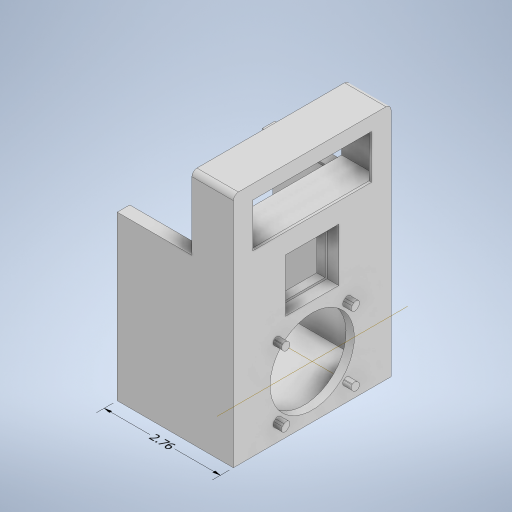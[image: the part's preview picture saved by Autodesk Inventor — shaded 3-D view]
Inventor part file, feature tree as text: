
AUTODESK INVENTOR PART (.ipt)
format: ipt  version: 2024 (Build 280153000, 153)  size: 946,688 bytes
history: native  units: in
note: dims shown in document units (in); Inventor stores cm internally (conversion verified against a paired STEP export)
features: extrude x9, sketch x7, other x2, projected_geometry x2, shell x1, fillet x1
ambient origin geometry x8: Origin, YZ Plane, XZ Plane, XY Plane, X Axis, Y Axis, Z Axis, Center Point
bodies: Solid1 (feature_tree)
feature tree (22):
  other  "Annotations"
  sketch  "Sketch1"  dims[d0=2.0709in d1=2.0709in]
  extrude  "Extrusion1"  Depth=2.0709in
  extrude  "Extrusion2"  Depth=1.2598in
  extrude  "Extrusion4"  Depth=0.8268in
  extrude  "Extrusion5"  Depth=0.2126in
  extrude  "Extrusion6"  Depth=0.0787in
  shell  "Shell2"  Thickness=1.5748in
  extrude  "Extrusion7"  Depth=2.815in
  extrude  "Extrusion8"  Depth=2.7559in
  extrude  "Extrusion9"  Depth=2.7559in
  extrude  "Extrusion10"  Depth=1.7323in
  fillet  "Fillet1"  Radius=3.7402in
  sketch  "Sketch2"  dims[d2=1.2598in d3=1.2598in]
  sketch  "Sketch3"  dims[d4=2.0in d5=0.8268in]
  sketch  "Sketch4"  dims[d6=0.8268in d7=0.2126in]
  projected_geometry  "Projected Loop1"
  sketch  "Sketch5"  dims[d8=0.1732in d9=0.0787in d10=1.5748in d12=360.0deg]
  sketch  "Sketch6"  dims[d15=0.1969in d16=2.815in]
  projected_geometry  "Projected Loop2"
  sketch  "Sketch7"  dims[d17=1.0433in d18=1.8701in d19=1.8701in d20=1.7323in d21=3.7402in d22=2.7559in d23=0.0in d25=0.1969in d26=0.0in d27=3.3661in d28=1.1811in d31=0.0591in d32=0.0in d33=0.0591in d34=0.0in d35=0.9843in d36=0.0in d37=0.0492in d38=2.5591in d39=0.0in d40=2.4803in d41=0.0in d50=90.0deg d51=0.0492in d52=0.1969in d53=0.0in d54=3.1496in d55=0.1969in d56=0.0in d57=0.1181in d45=0.0in d46=0.3937in d47=2.7559in]
  other  "Linear Dimension 1"
